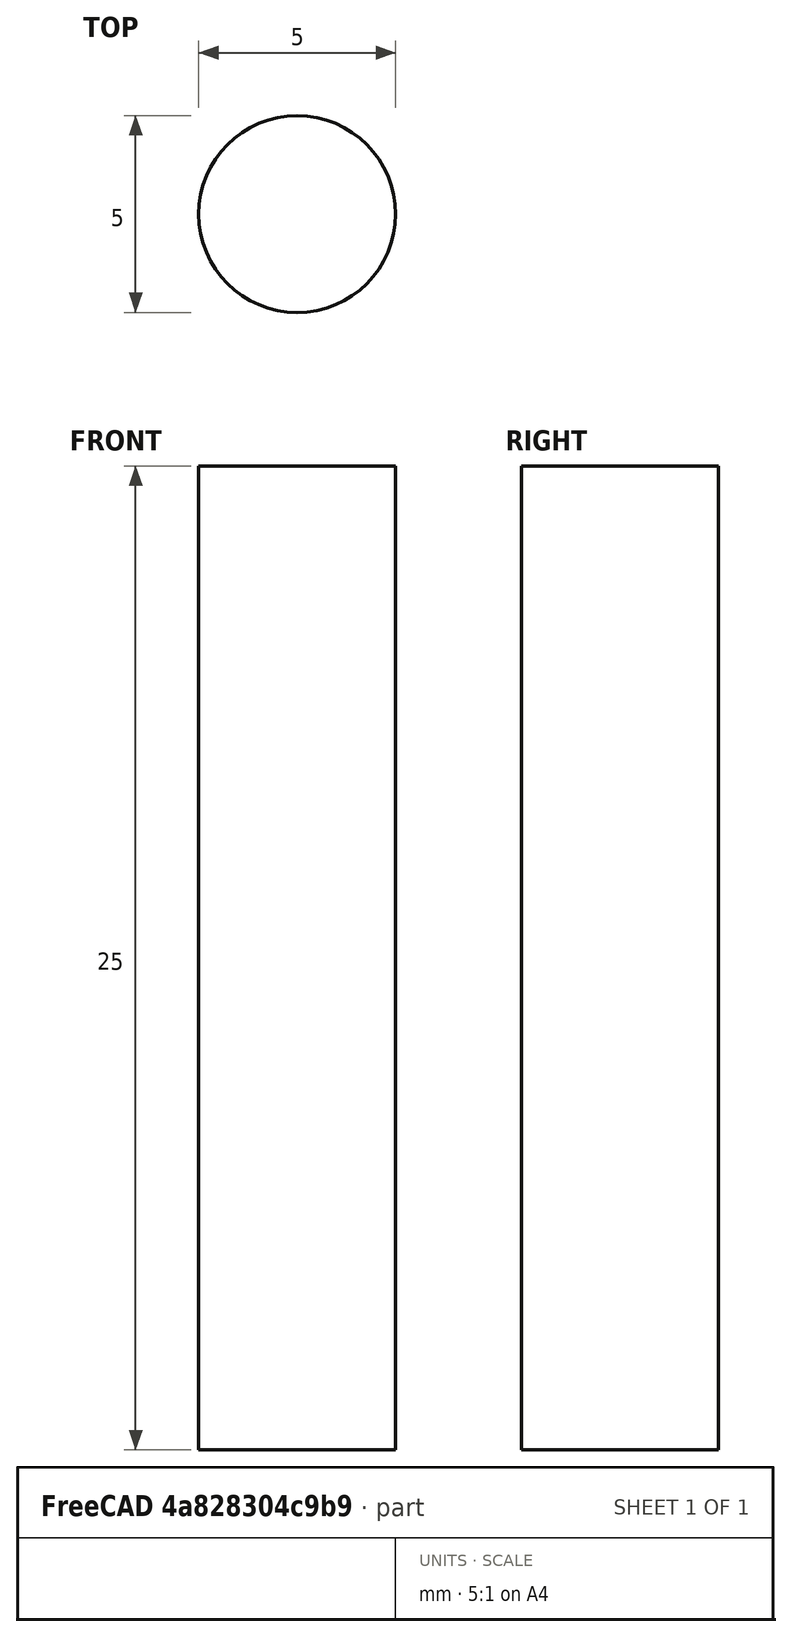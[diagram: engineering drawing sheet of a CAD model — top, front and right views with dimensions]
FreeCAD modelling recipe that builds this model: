
FCSTD DOCUMENT  (FreeCAD 1.0R39319 (Git))
Label: Assignment2_airpod_right
License: All rights reserved
LicenseURL: https://en.wikipedia.org/wiki/All_rights_reserved
objects: Sketcher::SketchObject×6, Part::FeaturePython×5, Part::Part2DObjectPython×2, Part::Loft×2, Part::Extrusion×2, Part::MultiFuse×2, Part::RuledSurface×2, Part::Revolution×1, PartDesign::SubShapeBinder×1, App::DocumentObjectGroup×1
note: 29 computed .brp shape members not serialized (recipe doc carries the construction recipe); baked Part::Feature solids carry a one-line shape summary decoded from their .brp

FEATURE [Sketcher::SketchObject] Sketch  label="Front_profile"
  ArcFitTolerance = 1e-06
  FullyConstrained = true
  MakeInternals = false
  Placement = pos=(0,0,0) rot=(1,0,0;1.5708rad)
  sketch-geometry (18):
    g0-g4: Circle [constr] x5 (B-spline internal-alignment scaffolding for g5; pole/knot coordinates omitted)
    g5: BSplineCurve PolesCount=5 KnotsCount=3 Degree=3 IsPeriodic=0
    g6: GeomPoint [constr] X=-2 Y=0 Z=0
    g7: GeomPoint [constr] X=0 Y=3.5 Z=0
    g8: GeomPoint [constr] X=2 Y=0 Z=0
    g9: BSplineCurve PolesCount=5 KnotsCount=3 Degree=3 IsPeriodic=0
    g10-g14: Circle [constr] x5 (B-spline internal-alignment scaffolding for g9; pole/knot coordinates omitted)
    g15: GeomPoint [constr] X=-2 Y=0 Z=0
    g16: GeomPoint [constr] X=0 Y=-3.5 Z=0
    g17: GeomPoint [constr] X=2 Y=0 Z=0
  constraints (21):
    c: Weight(g0) = 1
    c: Equal(g0, g1-g4) x4
    c: InternalAlignment(g0-g4 -> g5) x5
    c: InternalAlignment(g6,g5)
    c: InternalAlignment(g7,g5)
    c: InternalAlignment(g8,g5)
    c: Distance(g0,g1) = 3.5
    c: PointOnObject(g0,g-1)
    c: PointOnObject(g2,g-2)
    c: PointOnObject(g4,g-1)
    c: Horizontal(g1,g3)
    c: Coincident(g7,g2)
    c: Vertical(g3,g5)
    c: Vertical(g1,g5)
    c: DistanceX(g5,g5) = 4
    c: Weight(g10) = 1
    c: Equal(g10, g11-g14) x4
    c: InternalAlignment(g10-g17 -> g9) x8
    c: Distance(g10,g11) = 3.5
    c: Coincident(g16,g12)
    c: Block(g9)
FEATURE [Sketcher::SketchObject] Sketch001  label="mid_profile"
  ArcFitTolerance = 1e-06
  FullyConstrained = true
  MakeInternals = false
  Placement = pos=(0,8,0) rot=(1,0,0;1.5708rad)
  sketch-geometry (5):
    g0: Ellipse CenterX=0 CenterY=0 CenterZ=0 NormalX=0 NormalY=0 NormalZ=1 MajorRadius=10 MinorRadius=6 AngleXU=-1.5708
    g1: LineSegment [constr] StartX=-3.26795e-06 StartY=-10 StartZ=0 EndX=3.26795e-06 EndY=10 EndZ=0
    g2: LineSegment [constr] StartX=6 StartY=-1.96077e-06 StartZ=0 EndX=-6 EndY=1.96077e-06 EndZ=0
    g3: GeomPoint [constr] X=-2.61436e-06 Y=-8 Z=0
    g4: GeomPoint [constr] X=2.61436e-06 Y=8 Z=0
  constraints (5):
    c: InternalAlignment(g1-g4 -> g0) x4
    c: Distance(g0,g1) = 10
    c: Angle(g1) = 1.5708
    c: Distance(g0,g2) = 6
    c: Coincident(g0,g-1)
FEATURE [Part::Part2DObjectPython] Clone2D  label="End_profile"  # Draft 2D object (typed FeaturePython)
  Fuse = false
  Objects = -> [Sketch001]
  Placement = pos=(0,10,0) rot=(1,0,0;1.5708rad)
  Scale = (1,1,1)
FEATURE [Part::Loft] Loft
  Closed = false
  MaxDegree = 5
  Ruled = false
  Sections = -> [Sketch,Sketch001,Clone2D]
  Solid = false
FEATURE [Sketcher::SketchObject] Sketch002  label="end_profilehalf"
  ArcFitTolerance = 1e-06
  ExternalGeometry = -> [Loft]
  FullyConstrained = true
  MakeInternals = false
  Placement = pos=(0,10,0) rot=(1,0,0;1.5708rad)
  sketch-geometry (5):
    g0: ArcOfEllipse CenterX=0 CenterY=0 CenterZ=0 NormalX=0 NormalY=0 NormalZ=1 MajorRadius=10 MinorRadius=6 AngleXU=-1.5708 StartAngle=1.5708 EndAngle=4.71239
    g1: LineSegment [constr] StartX=0 StartY=-10 StartZ=0 EndX=0 EndY=10 EndZ=0
    g2: LineSegment [constr] StartX=6 StartY=-1e-16 StartZ=0 EndX=-6 EndY=1e-16 EndZ=0
    g3: GeomPoint [constr] X=0 Y=-8 Z=0
    g4: GeomPoint [constr] X=0 Y=8 Z=0
  constraints (6):
    c: InternalAlignment(g1-g4 -> g0) x4
    c: Coincident(g0,g-1)
    c: Coincident(g0,g-3)
    c: PointOnObject(g0,g2)
    c: DistanceY(g-1,g1) = 10
    c: Vertical(g1)
FEATURE [Sketcher::SketchObject] Sketch003  label="Rev_axis_endproflie"
  ArcFitTolerance = 1e-06
  ExternalGeometry = -> [Loft]
  FullyConstrained = true
  MakeInternals = false
  sketch-geometry (1):
    g0: LineSegment StartX=-6 StartY=10 StartZ=0 EndX=6 EndY=10 EndZ=0
  constraints (2):
    c: Coincident(g0,g-3)
    c: Coincident(g0,g-4)
FEATURE [Part::Revolution] Revolve
  Angle = -180
  Axis = (1,0,0)
  AxisLink = -> Sketch003 [Edge1]
  Base = (6,10,0)
  FaceMakerClass = Part::FaceMakerBullseye
  Solid = false
  Source = -> Sketch002
  Symmetric = false
FEATURE [Sketcher::SketchObject] Sketch004
  ArcFitTolerance = 1e-06
  FullyConstrained = false
  MakeInternals = false
  sketch-geometry (9):
    g0-g4: Circle [constr] x5 (B-spline internal-alignment scaffolding for g5; pole/knot coordinates omitted)
    g5: BSplineCurve PolesCount=5 KnotsCount=3 Degree=3 IsPeriodic=0
    g6: GeomPoint [constr] X=-5.70514 Y=20.576 Z=0
    g7: GeomPoint [constr] X=-2.13381 Y=8.65962 Z=0
    g8: GeomPoint [constr] X=-5.35982 Y=-3.17422 Z=0
  constraints (6):
    c: Weight(g0) = 1
    c: Equal(g0, g1-g4) x4
    c: InternalAlignment(g0-g4 -> g5) x5
    c: InternalAlignment(g6,g5)
    c: InternalAlignment(g7,g5)
    c: InternalAlignment(g8,g5)
FEATURE [Part::Extrusion] Extrude
  Base = -> Sketch004
  Dir = (0,0,1)
  DirMode = 2
  FaceMakerClass = Part::FaceMakerBullseye
  FaceMakerMode = 3
  LengthFwd = 20
  LengthRev = 0
  Solid = false
  Symmetric = true
FEATURE [Part::MultiFuse] Fusion
  Refine = true
  Shapes = -> [Loft,Revolve]
FEATURE [Part::FeaturePython] Slice  # WARN: FeaturePython — macro-defined, semantics opaque (R4)
  Base = -> Fusion
  Mode = 1
  Tolerance = 0
  Tools = -> [Extrude]
FEATURE [Part::FeaturePython] Slice_child0  label="Slice.0"  # WARN: FeaturePython — macro-defined, semantics opaque (R4)
  Base = -> Slice
  FilterType = 1
  Invert = false
  OverrideMaxVal = 0
  WindowFrom = 80
  WindowTo = 100
  items = 0
FEATURE [Part::FeaturePython] Slice_child1  label="Slice.1"  # WARN: FeaturePython — macro-defined, semantics opaque (R4)
  Base = -> Slice
  FilterType = 1
  Invert = false
  OverrideMaxVal = 0
  WindowFrom = 80
  WindowTo = 100
  items = 1
FEATURE [Part::FeaturePython] Slice_child2  label="Slice.2"  # WARN: FeaturePython — macro-defined, semantics opaque (R4)
  Base = -> Slice
  FilterType = 1
  Invert = false
  OverrideMaxVal = 0
  WindowFrom = 80
  WindowTo = 100
  items = 2
FEATURE [Part::FeaturePython] Slice_child3  label="Slice.3"  # WARN: FeaturePython — macro-defined, semantics opaque (R4)
  Base = -> Slice
  FilterType = 1
  Invert = false
  OverrideMaxVal = 0
  WindowFrom = 80
  WindowTo = 100
  items = 3
FEATURE [Sketcher::SketchObject] Sketch005  label="Stem_profile"
  ArcFitTolerance = 1e-06
  FullyConstrained = true
  MakeInternals = false
  Placement = pos=(0,0,-5) rot=(0,0,1;0rad)
  sketch-geometry (1):
    g0: Circle CenterX=-10 CenterY=12 CenterZ=0 NormalX=0 NormalY=0 NormalZ=1 AngleXU=0 Radius=2.5
  constraints (3):
    c: Diameter(g0) = 5
    c: DistanceX(g0,g-1) = 10
    c: DistanceY(g-1,g0) = 12
FEATURE [Part::Extrusion] Extrude001
  Base = -> Sketch005
  Dir = (0,0,1)
  DirMode = 2
  FaceMakerClass = Part::FaceMakerBullseye
  FaceMakerMode = 3
  LengthFwd = -25
  LengthRev = 0
  Solid = true
  Symmetric = false
FEATURE [Part::Part2DObjectPython] Clone2D001  label="Stem_profile (2D)"  # Draft 2D object (typed FeaturePython)
  Fuse = false
  Objects = -> [Sketch005]
  Placement = pos=(-0.5,0,-5.86603) rot=(0,1,0;0.523599rad)
  Scale = (1,1,1)
FEATURE [PartDesign::SubShapeBinder] Binder
  BindCopyOnChange = 0
  BindMode = 0
  ClaimChildren = false
  Fuse = false
  MakeFace = true
  OffsetFill = false
  OffsetIntersection = false
  OffsetJoinType = 0
  OffsetOpenResult = false
  PartialLoad = false
  Refine = true
  Relative = true
  Support = -> [Slice_child2[Edge2],Slice_child0[Edge2,Edge10]]
  _Version = 2
FEATURE [Part::Loft] Loft001
  Closed = false
  MaxDegree = 5
  Ruled = false
  Sections = -> [Sketch005,Clone2D001,Binder]
  Solid = false
FEATURE [Part::RuledSurface] Ruled_Surface
  Curve1 = -> Slice_child0 [Edge6]
  Curve2 = -> Slice_child0 [Edge5]
  Orientation = 0
FEATURE [Part::RuledSurface] Ruled_Surface001
  Curve1 = -> Ruled_Surface [Edge2]
  Curve2 = -> Slice_child0 [Edge11]
  Orientation = 0
FEATURE [Part::MultiFuse] Fusion001
  Refine = true
  Shapes = -> [Loft001,Slice_child0,Ruled_Surface,Ruled_Surface001,Slice_child2]
FEATURE [App::DocumentObjectGroup] GrExplode_Slice  label="Exploded Slice"
  Group = -> [Slice_child1,Slice_child3,Fusion001]
